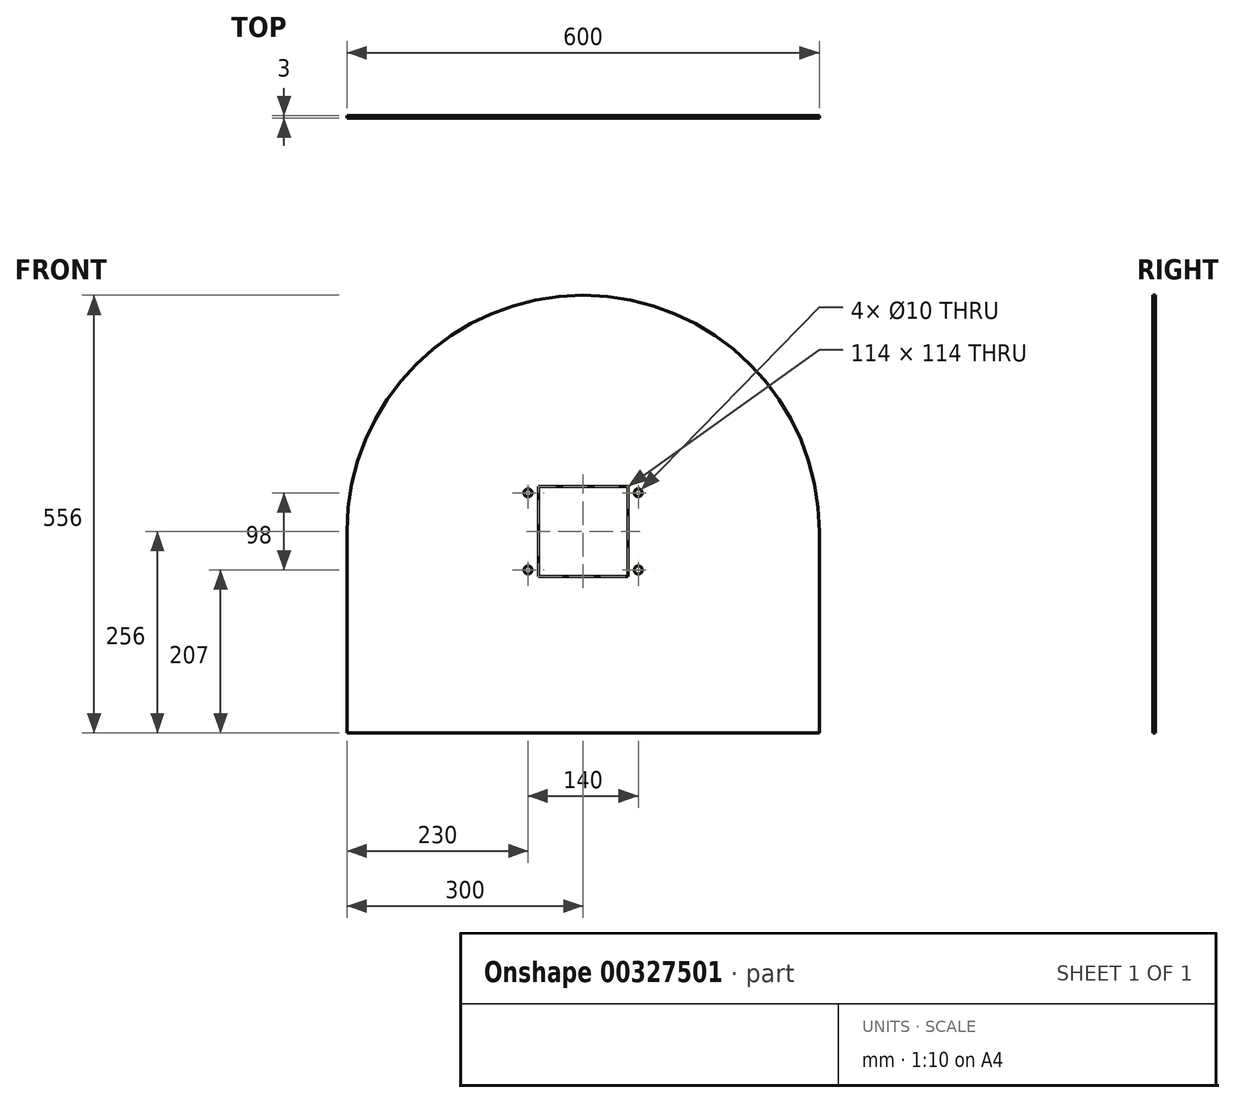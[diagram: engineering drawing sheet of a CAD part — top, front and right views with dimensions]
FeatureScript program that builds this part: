
annotation { "Feature Type Name" : "Feature", "Feature Type Description" : "" }
export const myFeature = defineFeature(function(context is Context, id is Id, definition is map)
    precondition{}
    {
        {
            var Q0;
            Q0=qCreatedBy(makeId("Front.planeOp"),FACE);
            var sketch = newSketch(context, id + "F0", { "sketchPlane" : qUnion([Q0])});
            skLineSegment(sketch, "E0.bottom", {"start": v(-300, -128) * mm, "end": v(300, -128) * mm});
            skLineSegment(sketch, "E0.top", {"start": v(-300, 128) * mm, "end": v(300, 128) * mm});
            skLineSegment(sketch, "E0.left", {"start": v(-300, -128) * mm, "end": v(-300, 128) * mm});
            skLineSegment(sketch, "E0.right", {"start": v(300, -128) * mm, "end": v(300, 128) * mm});
            skPoint(sketch, "E0.middle", {"position": v(0, 0) * mm});
            skPoint(sketch, "E1.endSnap0", {"position": v(0, 128) * mm});
            skArc(sketch, "E2", {"start": v(300, 128) * mm, "mid": v(0, 428) * mm, "end": v(-300, 128) * mm});
            skLineSegment(sketch, "E3.bottom", {"start": v(-57, 71) * mm, "end": v(57, 71) * mm});
            skLineSegment(sketch, "E3.top", {"start": v(-57, 185) * mm, "end": v(57, 185) * mm});
            skLineSegment(sketch, "E3.left", {"start": v(-57, 71) * mm, "end": v(-57, 185) * mm});
            skLineSegment(sketch, "E3.right", {"start": v(57, 71) * mm, "end": v(57, 185) * mm});
            skPoint(sketch, "E4.endSnap0", {"position": v(0, 185) * mm});
            skLineSegment(sketch, "E5", {"start": v(0, 177) * mm, "end": v(70, 177) * mm});
            skLineSegment(sketch, "E6", {"start": v(0, 177) * mm, "end": v(-70, 177) * mm});
            skPoint(sketch, "E7.endSnap0", {"position": v(0, 71) * mm});
            skLineSegment(sketch, "E8", {"start": v(0, 79) * mm, "end": v(70, 79) * mm});
            skLineSegment(sketch, "E9", {"start": v(0, 79) * mm, "end": v(-70, 79) * mm});
            skLineSegment(sketch, "E10", {"start": v(0, 128) * mm, "end": v(0, 79) * mm});
            skLineSegment(sketch, "E11", {"start": v(0, 128) * mm, "end": v(0, 177) * mm});
            skCircle(sketch, "E12", {"center": v(70, 79) * mm, "radius": 5 * mm});
            skCircle(sketch, "E13", {"center": v(70, 177) * mm, "radius": 5 * mm});
            skCircle(sketch, "E14", {"center": v(-70, 177) * mm, "radius": 5 * mm});
            skCircle(sketch, "E15", {"center": v(-70, 79) * mm, "radius": 5 * mm});
            skSolve(sketch);
        }
        {
            var Q0;
            Q0 = qSketchRegion(id + "F0", true);
            extrude(context, id + "F1", {"entities" : qUnion([Q0]), "depth" : 3 * mm});
        }
    });
